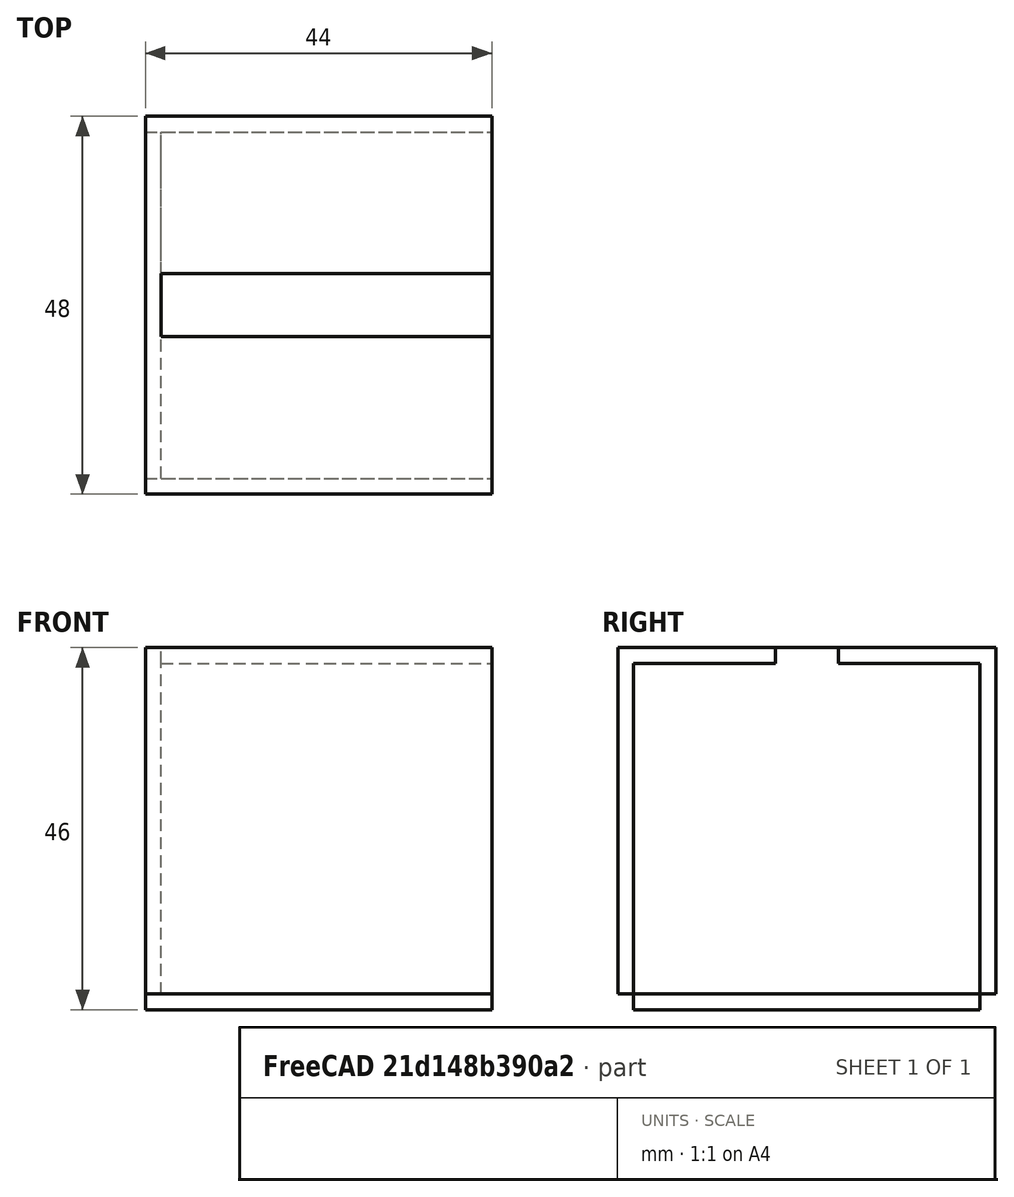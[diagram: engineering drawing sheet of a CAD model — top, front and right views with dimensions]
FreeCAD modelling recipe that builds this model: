
FCSTD DOCUMENT  (FreeCAD 0.20R29410 (Git))
Label: cajaaa
License: All rights reserved
LicenseURL: http://en.wikipedia.org/wiki/All_rights_reserved
objects: Part::Box×6, Part::MultiFuse×2, Part::Cut×1
note: 9 computed .brp shape members not serialized (recipe doc carries the construction recipe); baked Part::Feature solids carry a one-line shape summary decoded from their .brp

FEATURE [Part::Box] Box  label="Cubo"
  AttacherType = Attacher::AttachEngine3D
  Height = 44
  Length = 2
  Width = 44
FEATURE [Part::Box] Box001  label="Cubo001"
  AttacherType = Attacher::AttachEngine3D
  Height = 44
  Length = 2
  Placement = pos=(0,0,0) rot=(0,0,-1;1.5708rad)
  Width = 44
FEATURE [Part::Box] Box002  label="Cubo002"
  AttacherType = Attacher::AttachEngine3D
  Height = 44
  Length = 2
  Placement = pos=(0,46,0) rot=(0,0,-1;1.5708rad)
  Width = 44
FEATURE [Part::Box] Box003  label="Cubo003"
  AttacherType = Attacher::AttachEngine3D
  Height = 44
  Length = 2
  Placement = pos=(0,0,0) rot=(0,1,0;1.5708rad)
  Width = 44
FEATURE [Part::MultiFuse] Fusion
  Shapes = -> [Box,Box001,Box002,Box003]
FEATURE [Part::Box] Box004  label="Cubo004"
  AttacherType = Attacher::AttachEngine3D
  Height = 2
  Length = 42
  Placement = pos=(2,0,42) rot=(0,0,1;0rad)
  Width = 44
FEATURE [Part::Box] Box005  label="Cubo005"
  AttacherType = Attacher::AttachEngine3D
  Height = 2
  Length = 42
  Placement = pos=(2,18,42) rot=(0,0,1;0rad)
  Width = 8
FEATURE [Part::Cut] Cut
  Base = -> Box004
  Tool = -> Box005
FEATURE [Part::MultiFuse] Fusion002
  Shapes = -> [Fusion,Cut]
